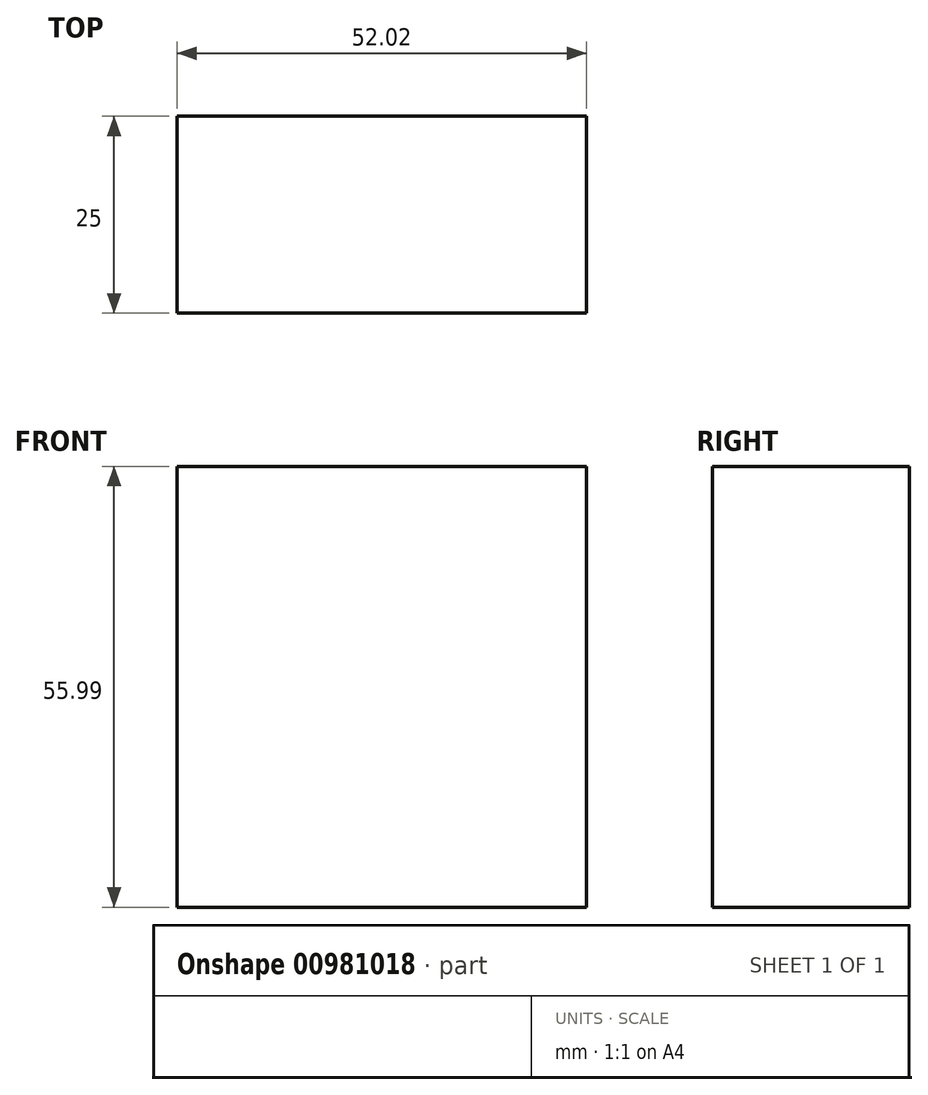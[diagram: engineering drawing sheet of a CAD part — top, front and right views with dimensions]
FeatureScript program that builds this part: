
annotation { "Feature Type Name" : "Feature", "Feature Type Description" : "" }
export const myFeature = defineFeature(function(context is Context, id is Id, definition is map)
    precondition{}
    {
        {
            var Q0;
            Q0=qCreatedBy(makeId("Front.planeOp"),FACE);
            var sketch = newSketch(context, id + "F0", { "sketchPlane" : qUnion([Q0])});
            skLineSegment(sketch, "E0.bottom", {"start": v(-125.8, 43.02) * mm, "end": v(-73.79, 43.02) * mm});
            skLineSegment(sketch, "E0.top", {"start": v(-125.8, -12.97) * mm, "end": v(-73.79, -12.97) * mm});
            skLineSegment(sketch, "E0.left", {"start": v(-125.8, 43.02) * mm, "end": v(-125.8, -12.97) * mm});
            skLineSegment(sketch, "E0.right", {"start": v(-73.79, 43.02) * mm, "end": v(-73.79, -12.97) * mm});
            skSolve(sketch);
        }
        {
            var Q0;
            Q0 = qSketchRegion(id + "F0", true);
            extrude(context, id + "F1", {"entities" : qUnion([Q0]), "depth" : 25 * mm, "offsetDistance" : 25 * mm});
        }
    });
